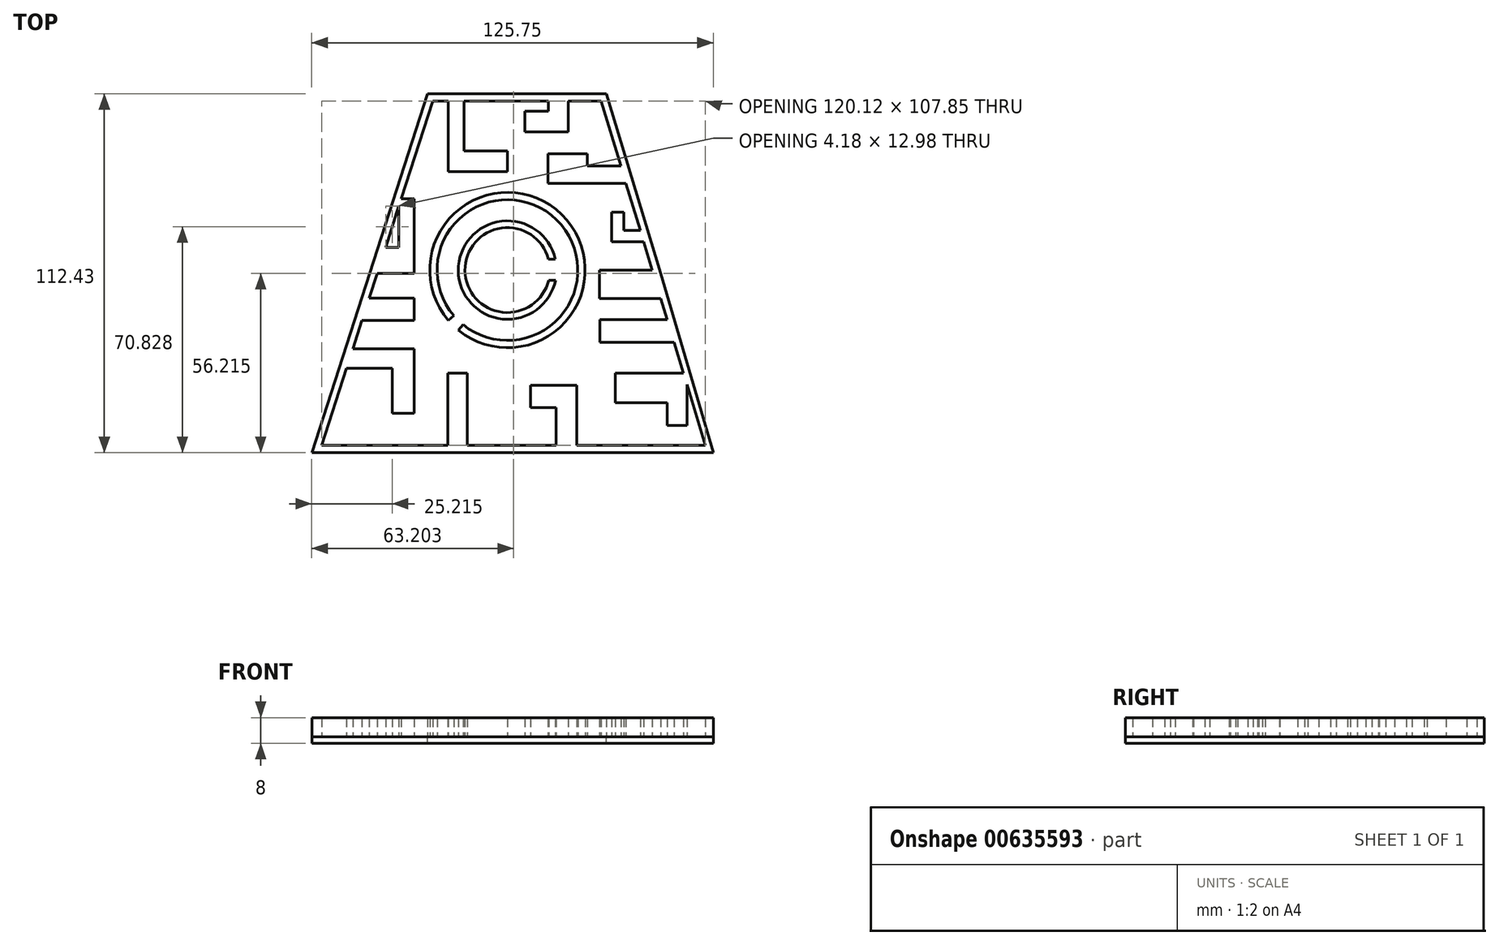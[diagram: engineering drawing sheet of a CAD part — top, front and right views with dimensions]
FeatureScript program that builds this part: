
annotation { "Feature Type Name" : "Feature", "Feature Type Description" : "" }
export const myFeature = defineFeature(function(context is Context, id is Id, definition is map)
    precondition{}
    {
        {
            var Q0;
            Q0=qCreatedBy(makeId("Top.planeOp"),FACE);
            var sketch = newSketch(context, id + "F0", { "sketchPlane" : qUnion([Q0])});
            skLineSegment(sketch, "E0", {"start": v(-58.15, -54.92) * mm, "end": v(-18.7, -54.92) * mm});
            skLineSegment(sketch, "E1", {"start": v(61.97, -54.92) * mm, "end": v(56.2, -35.84) * mm});
            skLineSegment(sketch, "E2", {"start": v(29.33, 52.93) * mm, "end": v(19.03, 52.93) * mm});
            skLineSegment(sketch, "E3", {"start": v(-23.41, 52.93) * mm, "end": v(-33.29, 22.28) * mm});
            skArc(sketch, "E4", {"start": v(-15.34, -18.87) * mm, "mid": v(17, 17.4) * mm, "end": v(-18.52, -15.77) * mm});
            skLineSegment(sketch, "E5.0", {"start": v(-25.08, 55.22) * mm, "end": v(-61.29, -57.2) * mm});
            skLineSegment(sketch, "E5.1", {"start": v(31.03, 55.22) * mm, "end": v(-25.08, 55.22) * mm});
            skLineSegment(sketch, "E5.2", {"start": v(48.04, -1) * mm, "end": v(31.03, 55.22) * mm});
            skLineSegment(sketch, "E5.3", {"start": v(-61.29, -57.2) * mm, "end": v(64.46, -57.2) * mm});
            skLineSegment(sketch, "E6", {"start": v(-48.4, -24.66) * mm, "end": v(-29.27, -24.66) * mm});
            skLineSegment(sketch, "E7", {"start": v(-29.27, -24.66) * mm, "end": v(-29.27, -44.89) * mm});
            skLineSegment(sketch, "E8", {"start": v(-29.27, -44.89) * mm, "end": v(-36.05, -44.89) * mm});
            skLineSegment(sketch, "E9", {"start": v(-36.05, -44.89) * mm, "end": v(-36.05, -30.78) * mm});
            skLineSegment(sketch, "E10", {"start": v(-36.05, -30.78) * mm, "end": v(-50.37, -30.78) * mm});
            skLineSegment(sketch, "E11", {"start": v(-45.54, -15.77) * mm, "end": v(-29.27, -15.77) * mm});
            skLineSegment(sketch, "E12", {"start": v(-29.27, -15.77) * mm, "end": v(-29.27, -8.81) * mm});
            skLineSegment(sketch, "E13", {"start": v(-29.27, -8.81) * mm, "end": v(-43.3, -8.81) * mm});
            skLineSegment(sketch, "E14", {"start": v(19.03, 52.93) * mm, "end": v(19.08, 43.27) * mm});
            skLineSegment(sketch, "E15", {"start": v(19.08, 43.27) * mm, "end": v(5.44, 43.27) * mm});
            skLineSegment(sketch, "E16", {"start": v(5.44, 43.27) * mm, "end": v(5.44, 49.77) * mm});
            skLineSegment(sketch, "E17", {"start": v(5.44, 49.77) * mm, "end": v(12.77, 49.77) * mm});
            skLineSegment(sketch, "E18", {"start": v(12.77, 49.77) * mm, "end": v(12.77, 52.93) * mm});
            skLineSegment(sketch, "E19", {"start": v(-13.53, 52.93) * mm, "end": v(-13.53, 37.32) * mm});
            skLineSegment(sketch, "E20", {"start": v(-13.53, 37.32) * mm, "end": v(0, 37.32) * mm});
            skLineSegment(sketch, "E21", {"start": v(-18.52, 52.93) * mm, "end": v(-18.52, 30.9) * mm});
            skLineSegment(sketch, "E22", {"start": v(-18.52, 30.9) * mm, "end": v(0, 30.9) * mm});
            skLineSegment(sketch, "E23", {"start": v(0, 30.9) * mm, "end": v(0, 37.32) * mm});
            skLineSegment(sketch, "E24", {"start": v(-40.78, -1) * mm, "end": v(-29.27, -1) * mm});
            skLineSegment(sketch, "E25", {"start": v(-29.27, -1) * mm, "end": v(-29.27, 22.28) * mm});
            skLineSegment(sketch, "E26", {"start": v(-29.27, 22.28) * mm, "end": v(-33.29, 22.28) * mm});
            skLineSegment(sketch, "E27", {"start": v(-33.99, 20.1) * mm, "end": v(-33.99, 7.13) * mm});
            skLineSegment(sketch, "E28", {"start": v(-33.99, 7.13) * mm, "end": v(-38.17, 7.13) * mm});
            skLineSegment(sketch, "E29", {"start": v(-18.7, -54.92) * mm, "end": v(-18.7, -32.29) * mm});
            skLineSegment(sketch, "E30", {"start": v(-18.7, -32.29) * mm, "end": v(-12.6, -32.29) * mm});
            skLineSegment(sketch, "E31", {"start": v(-12.6, -32.29) * mm, "end": v(-12.6, -54.92) * mm});
            skLineSegment(sketch, "E32", {"start": v(55.12, -32.29) * mm, "end": v(33.78, -32.29) * mm});
            skLineSegment(sketch, "E33", {"start": v(33.78, -32.29) * mm, "end": v(33.78, -41.54) * mm});
            skLineSegment(sketch, "E34", {"start": v(33.78, -41.54) * mm, "end": v(50, -41.54) * mm});
            skLineSegment(sketch, "E35", {"start": v(50, -41.54) * mm, "end": v(50, -48.69) * mm});
            skLineSegment(sketch, "E36", {"start": v(50, -48.69) * mm, "end": v(56.2, -48.69) * mm});
            skLineSegment(sketch, "E37", {"start": v(56.2, -48.69) * mm, "end": v(56.2, -35.84) * mm});
            skLineSegment(sketch, "E38", {"start": v(52.2, -22.6) * mm, "end": v(28.95, -22.6) * mm});
            skLineSegment(sketch, "E39", {"start": v(28.95, -22.6) * mm, "end": v(28.95, -15.48) * mm});
            skLineSegment(sketch, "E40", {"start": v(28.95, -15.48) * mm, "end": v(50.04, -15.48) * mm});
            skLineSegment(sketch, "E41", {"start": v(42.68, 8.83) * mm, "end": v(32.66, 8.83) * mm});
            skLineSegment(sketch, "E42", {"start": v(32.66, 8.83) * mm, "end": v(32.66, 18.13) * mm});
            skLineSegment(sketch, "E43", {"start": v(32.66, 18.13) * mm, "end": v(36.5, 18.13) * mm});
            skLineSegment(sketch, "E44", {"start": v(36.5, 18.13) * mm, "end": v(36.5, 12.42) * mm});
            skLineSegment(sketch, "E45", {"start": v(36.5, 12.42) * mm, "end": v(41.6, 12.42) * mm});
            skLineSegment(sketch, "E46", {"start": v(21.72, -54.92) * mm, "end": v(21.72, -36.06) * mm});
            skLineSegment(sketch, "E47", {"start": v(21.72, -36.06) * mm, "end": v(7.18, -36.06) * mm});
            skLineSegment(sketch, "E48", {"start": v(7.18, -36.06) * mm, "end": v(7.18, -43.02) * mm});
            skLineSegment(sketch, "E49", {"start": v(7.18, -43.02) * mm, "end": v(15.22, -43.02) * mm});
            skLineSegment(sketch, "E50", {"start": v(15.22, -43.02) * mm, "end": v(15.22, -54.92) * mm});
            skLineSegment(sketch, "E51", {"start": v(37.13, 27.15) * mm, "end": v(12.68, 27.15) * mm});
            skLineSegment(sketch, "E52", {"start": v(12.68, 27.15) * mm, "end": v(12.68, 36.37) * mm});
            skLineSegment(sketch, "E53", {"start": v(12.68, 36.37) * mm, "end": v(24.95, 36.37) * mm});
            skLineSegment(sketch, "E54", {"start": v(24.95, 36.37) * mm, "end": v(24.95, 32.56) * mm});
            skLineSegment(sketch, "E55", {"start": v(24.95, 32.56) * mm, "end": v(35.5, 32.56) * mm});
            skLineSegment(sketch, "E56", {"start": v(48.04, -8.89) * mm, "end": v(28.77, -8.89) * mm});
            skPoint(sketch, "E56.startSnap0", {"position": v(48.04, -1) * mm});
            skLineSegment(sketch, "E57", {"start": v(28.77, -8.89) * mm, "end": v(28.77, 0) * mm});
            skArc(sketch, "E58.0", {"start": v(-13.9, -17.1) * mm, "mid": v(15.4, 15.76) * mm, "end": v(-16.78, -14.28) * mm});
            skLineSegment(sketch, "E59", {"start": v(-16.78, -14.28) * mm, "end": v(-18.52, -15.77) * mm});
            skLineSegment(sketch, "E60", {"start": v(-13.9, -17.1) * mm, "end": v(-15.34, -18.87) * mm});
            skArc(sketch, "E61", {"start": v(15.02, 3.46) * mm, "mid": v(-15.41, -0.16) * mm, "end": v(15.09, -3.14) * mm});
            skArc(sketch, "E62.0", {"start": v(12.85, 3.46) * mm, "mid": v(-13.3, -0.16) * mm, "end": v(12.93, -3.14) * mm});
            skLineSegment(sketch, "E63", {"start": v(28.77, 0) * mm, "end": v(45.35, 0) * mm});
            skLineSegment(sketch, "E64.bottom", {"start": v(15.02, 3.46) * mm, "end": v(12.85, 3.46) * mm});
            skLineSegment(sketch, "E64.top", {"start": v(15.09, -3.14) * mm, "end": v(12.93, -3.14) * mm});
            skLineSegment(sketch, "E65.trimOffspring", {"start": v(-50.37, -30.78) * mm, "end": v(-58.15, -54.92) * mm});
            skLineSegment(sketch, "E66.trimOffspring", {"start": v(-12.6, -54.92) * mm, "end": v(15.22, -54.92) * mm});
            skLineSegment(sketch, "E67.trimOffspring", {"start": v(21.72, -54.92) * mm, "end": v(61.97, -54.92) * mm});
            skLineSegment(sketch, "E68.trimOffspring", {"start": v(-45.54, -15.77) * mm, "end": v(-48.4, -24.66) * mm});
            skLineSegment(sketch, "E69.trimOffspring", {"start": v(45.35, 0) * mm, "end": v(42.68, 8.83) * mm});
            skLineSegment(sketch, "E70.trimOffspring", {"start": v(50.04, -15.48) * mm, "end": v(48.04, -8.89) * mm});
            skLineSegment(sketch, "E71.trimOffspring", {"start": v(55.12, -32.29) * mm, "end": v(52.2, -22.6) * mm});
            skLineSegment(sketch, "E72.trimOffspring", {"start": v(41.6, 12.42) * mm, "end": v(37.13, 27.15) * mm});
            skLineSegment(sketch, "E73.trimOffspring", {"start": v(12.77, 52.93) * mm, "end": v(-13.53, 52.93) * mm});
            skLineSegment(sketch, "E74.trimOffspring", {"start": v(-18.52, 52.93) * mm, "end": v(-23.41, 52.93) * mm});
            skLineSegment(sketch, "E75.trimOffspring", {"start": v(-40.78, -1) * mm, "end": v(-43.3, -8.81) * mm});
            skLineSegment(sketch, "E76.trimOffspring", {"start": v(-33.99, 20.1) * mm, "end": v(-38.17, 7.13) * mm});
            skLineSegment(sketch, "E77", {"start": v(29.33, 52.93) * mm, "end": v(35.5, 32.56) * mm});
            skLineSegment(sketch, "E78", {"start": v(48.04, -1) * mm, "end": v(64.46, -57.2) * mm});
            skPoint(sketch, "E79.orphan", {"position": v(65.05, -59.24) * mm});
            skPoint(sketch, "E80.orphan", {"position": v(65.05, -57.2) * mm});
            skSolve(sketch);
        }
        {
            var Q0;
            Q0 = qSketchRegion(id + "F0", true);
            var Q1;
            Q1=makeQuery(id+"F0.imprint","IMPRINT",FACE,{"disambiguationData":[TD([[makeQuery(id+"F0.imprint","IMPRINT",EDGE,{"derivedFrom":sQuery(id+"F0.wireOp",EDGE,"E4")}),1.0]])]});
            var Q2;
            Q2=makeQuery(id+"F0.imprint","IMPRINT",FACE,{"disambiguationData":[TD([[makeQuery(id+"F0.imprint","IMPRINT",EDGE,{"derivedFrom":sQuery(id+"F0.wireOp",EDGE,"E61")}),1.0]])]});
            extrude(context, id + "F1", {"entities" : qUnion([Q0, Q1, Q2]), "depth" : 6 * mm, "offsetDistance" : 25 * mm});
        }
        {
            var Q0;
            Q0=qCreatedBy(makeId("Top.planeOp"),FACE);
            var sketch = newSketch(context, id + "F2", { "sketchPlane" : qUnion([Q0])});
            skLineSegment(sketch, "E81.0", {"start": v(-61.29, -57.2) * mm, "end": v(64.46, -57.2) * mm});
            skLineSegment(sketch, "E82.0", {"start": v(48.04, -1) * mm, "end": v(64.46, -57.2) * mm});
            skLineSegment(sketch, "E83.0", {"start": v(48.04, -1) * mm, "end": v(31.03, 55.22) * mm});
            skPoint(sketch, "E84.0", {"position": v(19.03, 52.93) * mm});
            skLineSegment(sketch, "E85.0", {"start": v(31.03, 55.22) * mm, "end": v(-25.08, 55.22) * mm});
            skLineSegment(sketch, "E86.0", {"start": v(-25.08, 55.22) * mm, "end": v(-61.29, -57.2) * mm});
            skSolve(sketch);
        }
        {
            var Q0;
            Q0 = qSketchRegion(id + "F2", true);
            extrude(context, id + "F3", {"entities" : qUnion([Q0]), "oppositeDirection" : true, "depth" : 2 * mm, "offsetDistance" : 25 * mm});
        }
    });
